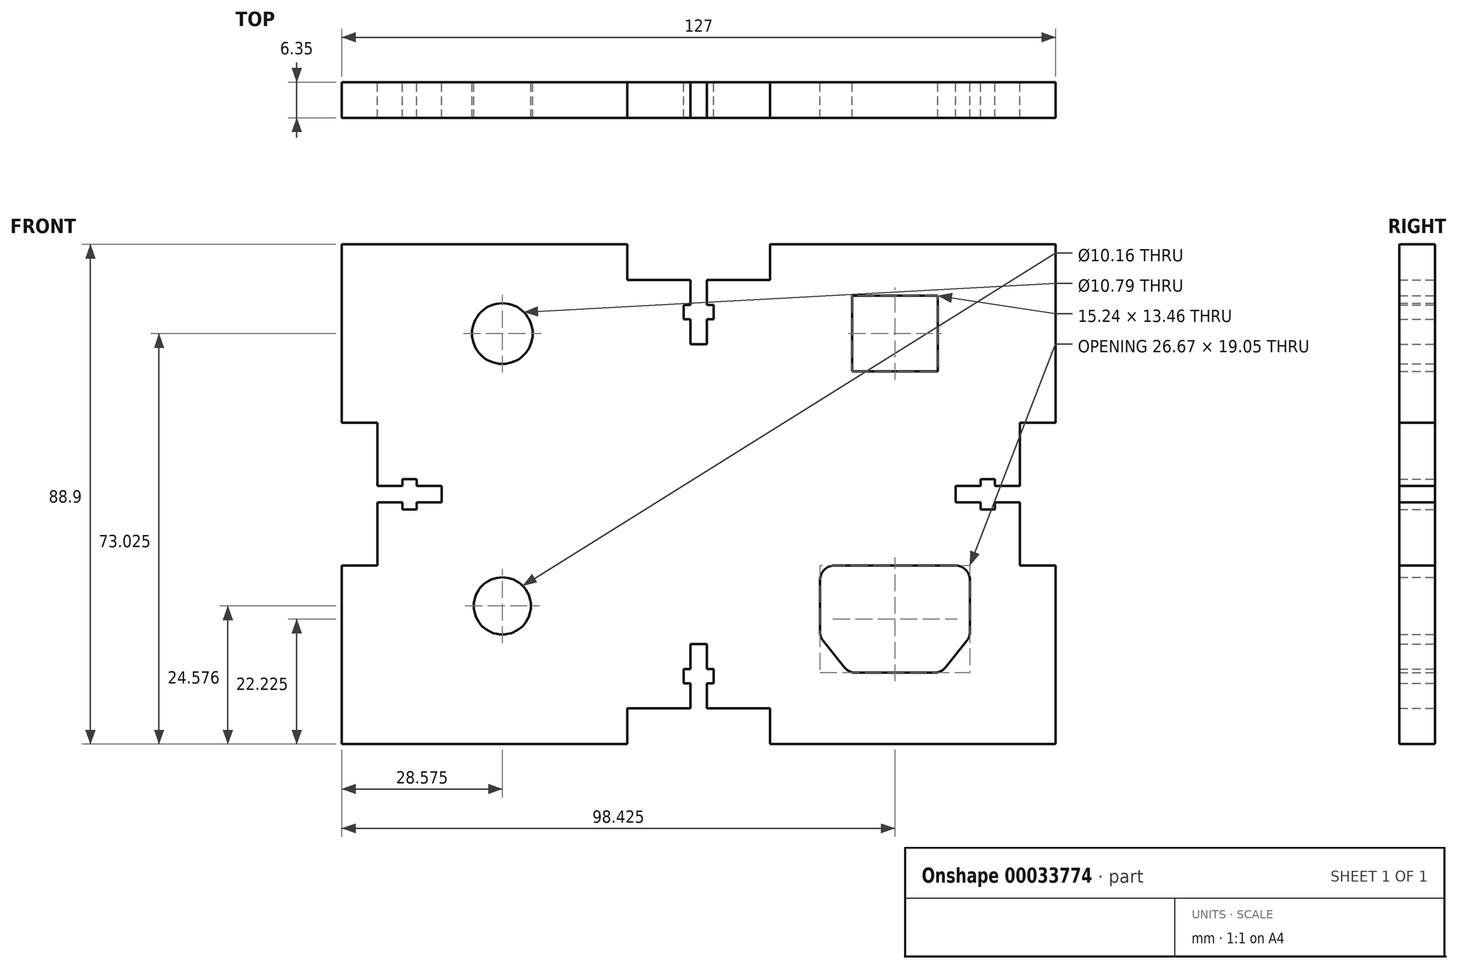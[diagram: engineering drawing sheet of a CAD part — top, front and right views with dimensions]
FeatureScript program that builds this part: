
annotation { "Feature Type Name" : "Feature", "Feature Type Description" : "" }
export const myFeature = defineFeature(function(context is Context, id is Id, definition is map)
    precondition{}
    {
        {
            var Q0;
            Q0=qCreatedBy(makeId("Front.planeOp"),FACE);
            var sketch = newSketch(context, id + "F0", { "sketchPlane" : qUnion([Q0])});
            skLineSegment(sketch, "E0.rect.bottom", {"start": v(57.15, -44.45) * mm, "end": v(12.7, -44.45) * mm});
            skLineSegment(sketch, "E0.rect.top", {"start": v(57.15, 44.45) * mm, "end": v(12.7, 44.45) * mm});
            skPoint(sketch, "E0.rect.middle", {"position": v(0, 0) * mm});
            skLineSegment(sketch, "E1.0", {"start": v(57.15, 38.1) * mm, "end": v(-57.15, 38.1) * mm, "construction": true});
            skLineSegment(sketch, "E1.1", {"start": v(57.15, -38.1) * mm, "end": v(57.15, 38.1) * mm, "construction": true});
            skLineSegment(sketch, "E1.2", {"start": v(57.15, -38.1) * mm, "end": v(-57.15, -38.1) * mm, "construction": true});
            skLineSegment(sketch, "E2", {"start": v(-63.5, 0) * mm, "end": v(-57.15, 0) * mm, "construction": true});
            skLineSegment(sketch, "E3", {"start": v(0, 44.45) * mm, "end": v(0, -44.45) * mm, "construction": true});
            skLineSegment(sketch, "E4.MirrorCS", {"start": v(12.7, 44.45) * mm, "end": v(12.7, -44.45) * mm, "construction": true});
            skLineSegment(sketch, "E5.0", {"start": v(-63.5, -12.7) * mm, "end": v(63.5, -12.7) * mm, "construction": true});
            skLineSegment(sketch, "E6.MirrorCS", {"start": v(-63.5, 12.7) * mm, "end": v(-57.15, 12.7) * mm, "construction": true});
            skLineSegment(sketch, "E7", {"start": v(-63.5, 12.7) * mm, "end": v(-57.15, 12.7) * mm});
            skLineSegment(sketch, "E8", {"start": v(-63.5, -12.7) * mm, "end": v(-57.15, -12.7) * mm});
            skPoint(sketch, "E9.orphan", {"position": v(-63.5, -44.45) * mm});
            skPoint(sketch, "E10.orphan", {"position": v(-63.5, 44.45) * mm});
            skLineSegment(sketch, "E11.MirrorCS", {"start": v(63.5, -12.7) * mm, "end": v(57.15, -12.7) * mm});
            skLineSegment(sketch, "E12.MirrorCS", {"start": v(63.5, 12.7) * mm, "end": v(57.15, 12.7) * mm});
            skPoint(sketch, "E13.orphan", {"position": v(63.5, 44.45) * mm});
            skPoint(sketch, "E14.orphan", {"position": v(63.5, -44.45) * mm});
            skLineSegment(sketch, "E15", {"start": v(-12.7, 44.45) * mm, "end": v(-12.7, 38.1) * mm});
            skLineSegment(sketch, "E16", {"start": v(-12.7, 38.1) * mm, "end": v(-1.46, 38.1) * mm});
            skLineSegment(sketch, "E17", {"start": v(12.7, 38.1) * mm, "end": v(12.7, 44.45) * mm});
            skLineSegment(sketch, "E18.MirrorCS", {"start": v(-12.7, -44.45) * mm, "end": v(-12.7, -38.1) * mm});
            skLineSegment(sketch, "E19.MirrorCS", {"start": v(-12.7, -38.1) * mm, "end": v(-1.46, -38.1) * mm});
            skLineSegment(sketch, "E20.MirrorCS", {"start": v(12.7, -38.1) * mm, "end": v(12.7, -44.45) * mm});
            skLineSegment(sketch, "E21.trimOffspring", {"start": v(-12.7, 44.45) * mm, "end": v(-57.15, 44.45) * mm});
            skLineSegment(sketch, "E22.trimOffspring", {"start": v(-12.7, -44.45) * mm, "end": v(-57.15, -44.45) * mm});
            skLineSegment(sketch, "E23", {"start": v(-12.7, 26.67) * mm, "end": v(12.7, 26.67) * mm, "construction": true});
            skLineSegment(sketch, "E24.0", {"start": v(-1.46, 44.45) * mm, "end": v(-1.46, -44.45) * mm, "construction": true});
            skLineSegment(sketch, "E25.0", {"start": v(-2.7, 44.45) * mm, "end": v(-2.7, -44.45) * mm, "construction": true});
            skLineSegment(sketch, "E26.MirrorCS", {"start": v(1.46, 44.45) * mm, "end": v(1.46, -44.45) * mm, "construction": true});
            skLineSegment(sketch, "E27.MirrorCS", {"start": v(2.7, 44.45) * mm, "end": v(2.7, -44.45) * mm, "construction": true});
            skLineSegment(sketch, "E28", {"start": v(-12.7, 26.67) * mm, "end": v(-12.7, -44.45) * mm, "construction": true});
            skLineSegment(sketch, "E29", {"start": v(-12.7, 38.1) * mm, "end": v(-12.7, 26.67) * mm, "construction": true});
            skLineSegment(sketch, "E30", {"start": v(-12.7, 32.39) * mm, "end": v(12.7, 32.39) * mm, "construction": true});
            skLineSegment(sketch, "E31.0", {"start": v(-12.7, 31.12) * mm, "end": v(12.7, 31.12) * mm, "construction": true});
            skLineSegment(sketch, "E32.MirrorCS", {"start": v(-12.7, 33.66) * mm, "end": v(12.7, 33.66) * mm, "construction": true});
            skLineSegment(sketch, "E33", {"start": v(-1.46, 38.1) * mm, "end": v(-1.46, 33.66) * mm});
            skPoint(sketch, "E33.endSnap0", {"position": v(0, 33.66) * mm});
            skLineSegment(sketch, "E34", {"start": v(-1.46, 33.66) * mm, "end": v(-2.7, 33.66) * mm});
            skLineSegment(sketch, "E35", {"start": v(-2.7, 33.66) * mm, "end": v(-2.7, 31.12) * mm});
            skLineSegment(sketch, "E36", {"start": v(-2.7, 31.12) * mm, "end": v(-1.46, 31.12) * mm});
            skLineSegment(sketch, "E37", {"start": v(-1.46, 31.12) * mm, "end": v(-1.46, 26.67) * mm});
            skLineSegment(sketch, "E38", {"start": v(-1.46, 26.67) * mm, "end": v(1.46, 26.67) * mm});
            skLineSegment(sketch, "E39", {"start": v(1.46, 26.67) * mm, "end": v(1.46, 31.12) * mm});
            skLineSegment(sketch, "E40", {"start": v(1.46, 31.12) * mm, "end": v(2.7, 31.12) * mm});
            skLineSegment(sketch, "E41", {"start": v(2.7, 31.12) * mm, "end": v(2.7, 33.66) * mm});
            skLineSegment(sketch, "E42", {"start": v(2.7, 33.66) * mm, "end": v(1.46, 33.66) * mm});
            skLineSegment(sketch, "E43", {"start": v(1.46, 33.66) * mm, "end": v(1.46, 38.1) * mm});
            skLineSegment(sketch, "E44.trimOffspring", {"start": v(1.46, 38.1) * mm, "end": v(12.7, 38.1) * mm});
            skLineSegment(sketch, "E45.MirrorCS", {"start": v(1.46, -33.66) * mm, "end": v(1.46, -38.1) * mm});
            skLineSegment(sketch, "E46.MirrorCS", {"start": v(2.7, -33.66) * mm, "end": v(1.46, -33.66) * mm});
            skLineSegment(sketch, "E47.MirrorCS", {"start": v(2.7, -31.12) * mm, "end": v(2.7, -33.66) * mm});
            skLineSegment(sketch, "E48.MirrorCS", {"start": v(1.46, -31.12) * mm, "end": v(2.7, -31.12) * mm});
            skLineSegment(sketch, "E49.MirrorCS", {"start": v(1.46, -26.67) * mm, "end": v(1.46, -31.12) * mm});
            skLineSegment(sketch, "E50.MirrorCS", {"start": v(-1.46, -26.67) * mm, "end": v(1.46, -26.67) * mm});
            skLineSegment(sketch, "E51.MirrorCS", {"start": v(-1.46, -31.12) * mm, "end": v(-1.46, -26.67) * mm});
            skLineSegment(sketch, "E52.MirrorCS", {"start": v(-2.7, -31.12) * mm, "end": v(-1.46, -31.12) * mm});
            skLineSegment(sketch, "E53.MirrorCS", {"start": v(-2.7, -33.66) * mm, "end": v(-2.7, -31.12) * mm});
            skLineSegment(sketch, "E54.MirrorCS", {"start": v(-1.46, -33.66) * mm, "end": v(-2.7, -33.66) * mm});
            skLineSegment(sketch, "E55.MirrorCS", {"start": v(-1.46, -38.1) * mm, "end": v(-1.46, -33.66) * mm});
            skLineSegment(sketch, "E56.trimOffspring", {"start": v(1.46, -38.1) * mm, "end": v(12.7, -38.1) * mm});
            skLineSegment(sketch, "E57", {"start": v(-57.15, 0) * mm, "end": v(-57.15, 38.1) * mm, "construction": true});
            skLineSegment(sketch, "E58", {"start": v(-34.93, 0) * mm, "end": v(63.5, 0) * mm, "construction": true});
            skLineSegment(sketch, "E59", {"start": v(-34.93, 44.45) * mm, "end": v(-34.93, -44.45) * mm, "construction": true});
            skLineSegment(sketch, "E60", {"start": v(34.93, 44.45) * mm, "end": v(34.93, -44.45) * mm});
            skLineSegment(sketch, "E61", {"start": v(-34.93, 28.57) * mm, "end": v(-57.15, 28.57) * mm, "construction": true});
            skPoint(sketch, "E61.startSnap0", {"position": v(-57.15, 28.57) * mm});
            skLineSegment(sketch, "E62", {"start": v(-34.93, 28.57) * mm, "end": v(57.15, 28.58) * mm, "construction": true});
            skLineSegment(sketch, "E63", {"start": v(57.15, -28.57) * mm, "end": v(-57.15, -28.58) * mm, "construction": true});
            skLineSegment(sketch, "E64.rect.bottom", {"start": v(42.55, 21.84) * mm, "end": v(27.3, 21.84) * mm});
            skLineSegment(sketch, "E64.rect.top", {"start": v(42.55, 35.3) * mm, "end": v(27.3, 35.3) * mm});
            skLineSegment(sketch, "E64.rect.left", {"start": v(42.55, 21.84) * mm, "end": v(42.55, 35.3) * mm});
            skLineSegment(sketch, "E64.rect.right", {"start": v(27.3, 21.84) * mm, "end": v(27.3, 35.3) * mm});
            skPoint(sketch, "E64.rect.middle", {"position": v(34.93, 28.58) * mm});
            skLineSegment(sketch, "E65", {"start": v(24.13, -12.7) * mm, "end": v(45.72, -12.7) * mm});
            skLineSegment(sketch, "E66", {"start": v(48.26, -15.24) * mm, "end": v(48.26, -24.5) * mm});
            skLineSegment(sketch, "E67.MirrorCS", {"start": v(21.6, -15.24) * mm, "end": v(21.6, -24.5) * mm});
            skLineSegment(sketch, "E68", {"start": v(21.6, -25.4) * mm, "end": v(48.26, -25.4) * mm, "construction": true});
            skLineSegment(sketch, "E69.0", {"start": v(34.93, -31.75) * mm, "end": v(41.96, -31.75) * mm});
            skLineSegment(sketch, "E70", {"start": v(43.94, -30.8) * mm, "end": v(47.7, -26.1) * mm});
            skLineSegment(sketch, "E71.MirrorCS", {"start": v(34.93, -31.75) * mm, "end": v(27.9, -31.75) * mm});
            skLineSegment(sketch, "E72.MirrorCS", {"start": v(25.9, -30.8) * mm, "end": v(22.15, -26.1) * mm});
            skPoint(sketch, "E73.visualSharp", {"position": v(21.6, -12.7) * mm});
            skArc(sketch, "E73.filletArc", {"start": v(24.13, -12.7) * mm, "mid": v(22.33, -13.44) * mm, "end": v(21.6, -15.24) * mm});
            skPoint(sketch, "E74.visualSharp", {"position": v(48.26, -12.7) * mm});
            skArc(sketch, "E74.filletArc", {"start": v(48.26, -15.24) * mm, "mid": v(47.52, -13.44) * mm, "end": v(45.72, -12.7) * mm});
            skPoint(sketch, "E75.visualSharp", {"position": v(48.26, -25.4) * mm});
            skArc(sketch, "E75.filletArc", {"start": v(47.7, -26.1) * mm, "mid": v(48.12, -25.35) * mm, "end": v(48.26, -24.5) * mm});
            skPoint(sketch, "E76.visualSharp", {"position": v(43.18, -31.75) * mm});
            skArc(sketch, "E76.filletArc", {"start": v(41.96, -31.75) * mm, "mid": v(43.06, -31.5) * mm, "end": v(43.94, -30.8) * mm});
            skPoint(sketch, "E77.visualSharp", {"position": v(26.67, -31.75) * mm});
            skArc(sketch, "E77.filletArc", {"start": v(25.9, -30.8) * mm, "mid": v(26.8, -31.5) * mm, "end": v(27.9, -31.75) * mm});
            skPoint(sketch, "E78.visualSharp", {"position": v(21.6, -25.4) * mm});
            skArc(sketch, "E78.filletArc", {"start": v(21.6, -24.5) * mm, "mid": v(21.73, -25.35) * mm, "end": v(22.15, -26.1) * mm});
            skCircle(sketch, "E79", {"center": v(-34.93, 28.57) * mm, "radius": 5.4 * mm});
            skLineSegment(sketch, "E80", {"start": v(21.6, -19.87) * mm, "end": v(-34.93, -19.87) * mm, "construction": true});
            skCircle(sketch, "E81", {"center": v(-34.93, -19.87) * mm, "radius": 5.08 * mm});
            skLineSegment(sketch, "E82", {"start": v(-57.15, 44.45) * mm, "end": v(-63.5, 44.45) * mm});
            skLineSegment(sketch, "E83", {"start": v(-63.5, 12.7) * mm, "end": v(-63.5, 44.45) * mm});
            skLineSegment(sketch, "E84", {"start": v(-63.5, -12.7) * mm, "end": v(-63.5, -44.45) * mm});
            skLineSegment(sketch, "E85", {"start": v(-57.15, -44.45) * mm, "end": v(-63.5, -44.45) * mm});
            skLineSegment(sketch, "E86", {"start": v(57.15, -44.45) * mm, "end": v(63.5, -44.45) * mm});
            skLineSegment(sketch, "E87", {"start": v(63.5, -44.45) * mm, "end": v(63.5, -12.7) * mm});
            skLineSegment(sketch, "E88", {"start": v(63.5, 12.7) * mm, "end": v(63.5, 44.45) * mm});
            skLineSegment(sketch, "E89", {"start": v(63.5, 44.45) * mm, "end": v(57.15, 44.45) * mm});
            skLineSegment(sketch, "E90", {"start": v(-57.15, -12.7) * mm, "end": v(-57.15, -2.7) * mm});
            skPoint(sketch, "E91.center.orphan", {"position": v(-60.33, 0) * mm});
            skLineSegment(sketch, "E92", {"start": v(57.15, 12.7) * mm, "end": v(57.15, 1.46) * mm});
            skPoint(sketch, "E93.MirrorCS.end.orphan", {"position": v(57.15, 12.7) * mm});
            skPoint(sketch, "E93.MirrorCS.start.orphan", {"position": v(50.8, 12.7) * mm});
            skPoint(sketch, "E94.MirrorCS.start.orphan", {"position": v(50.8, -12.7) * mm});
            skPoint(sketch, "E95.orphan", {"position": v(57.15, -12.7) * mm});
            skPoint(sketch, "E96.MirrorCS.end.orphan", {"position": v(63.5, 12.7) * mm});
            skPoint(sketch, "E97.MirrorCS.start.orphan", {"position": v(-50.8, -12.7) * mm});
            skPoint(sketch, "E98.MirrorCS.end.orphan", {"position": v(-57.15, 12.7) * mm});
            skPoint(sketch, "E99.MirrorCS.end.orphan", {"position": v(-57.15, -12.7) * mm});
            skLineSegment(sketch, "E100", {"start": v(-34.93, 0) * mm, "end": v(-57.15, 0) * mm, "construction": true});
            skLineSegment(sketch, "E101.0", {"start": v(-34.93, 1.46) * mm, "end": v(-57.15, 1.46) * mm, "construction": true});
            skLineSegment(sketch, "E102.MirrorCS", {"start": v(-34.93, -1.46) * mm, "end": v(-57.15, -1.46) * mm, "construction": true});
            skLineSegment(sketch, "E103.0", {"start": v(-34.93, 2.7) * mm, "end": v(-57.15, 2.7) * mm, "construction": true});
            skLineSegment(sketch, "E104.MirrorCS", {"start": v(-34.93, -2.7) * mm, "end": v(-57.15, -2.7) * mm, "construction": true});
            skLineSegment(sketch, "E105", {"start": v(-45.72, 12.7) * mm, "end": v(-45.72, -12.7) * mm, "construction": true});
            skLineSegment(sketch, "E106.trimOffspring", {"start": v(-45.72, 12.7) * mm, "end": v(63.5, 12.7) * mm, "construction": true});
            skLineSegment(sketch, "E107", {"start": v(-57.15, 12.7) * mm, "end": v(-45.72, 12.7) * mm, "construction": true});
            skLineSegment(sketch, "E108", {"start": v(-52.7, -1.46) * mm, "end": v(-57.15, -1.46) * mm});
            skLineSegment(sketch, "E109.trimOffspring", {"start": v(-57.15, 1.46) * mm, "end": v(-57.15, 12.7) * mm});
            skLineSegment(sketch, "E110", {"start": v(-57.15, -1.46) * mm, "end": v(-57.15, -2.7) * mm});
            skLineSegment(sketch, "E111.trimOffspring", {"start": v(57.15, -1.46) * mm, "end": v(57.15, -12.7) * mm});
            skLineSegment(sketch, "E112", {"start": v(-51.44, 12.7) * mm, "end": v(-51.44, -12.7) * mm, "construction": true});
            skLineSegment(sketch, "E113.0", {"start": v(-52.7, 12.7) * mm, "end": v(-52.7, -12.7) * mm, "construction": true});
            skLineSegment(sketch, "E114.MirrorCS", {"start": v(-50.17, 12.7) * mm, "end": v(-50.17, -12.7) * mm, "construction": true});
            skLineSegment(sketch, "E115", {"start": v(-57.15, 1.46) * mm, "end": v(-52.7, 1.46) * mm});
            skLineSegment(sketch, "E116", {"start": v(-52.7, 1.46) * mm, "end": v(-52.7, 2.7) * mm});
            skLineSegment(sketch, "E117", {"start": v(-52.7, 2.7) * mm, "end": v(-50.17, 2.7) * mm});
            skLineSegment(sketch, "E118", {"start": v(-50.17, 2.7) * mm, "end": v(-50.17, 1.46) * mm});
            skLineSegment(sketch, "E119", {"start": v(-50.17, 1.46) * mm, "end": v(-45.72, 1.46) * mm});
            skLineSegment(sketch, "E120", {"start": v(-45.72, 1.46) * mm, "end": v(-45.72, -1.46) * mm});
            skLineSegment(sketch, "E121", {"start": v(-45.72, -1.46) * mm, "end": v(-50.17, -1.46) * mm});
            skLineSegment(sketch, "E122", {"start": v(-50.17, -1.46) * mm, "end": v(-50.17, -2.7) * mm});
            skLineSegment(sketch, "E123", {"start": v(-50.17, -2.7) * mm, "end": v(-52.7, -2.7) * mm});
            skLineSegment(sketch, "E124", {"start": v(-52.7, -2.7) * mm, "end": v(-52.7, -1.46) * mm});
            skLineSegment(sketch, "E125.MirrorCS", {"start": v(52.7, -1.46) * mm, "end": v(57.15, -1.46) * mm});
            skLineSegment(sketch, "E126.MirrorCS", {"start": v(52.7, -2.7) * mm, "end": v(52.7, -1.46) * mm});
            skLineSegment(sketch, "E127.MirrorCS", {"start": v(50.17, -2.7) * mm, "end": v(52.7, -2.7) * mm});
            skLineSegment(sketch, "E128.MirrorCS", {"start": v(50.17, -1.46) * mm, "end": v(50.17, -2.7) * mm});
            skLineSegment(sketch, "E129.MirrorCS", {"start": v(45.72, -1.46) * mm, "end": v(50.17, -1.46) * mm});
            skLineSegment(sketch, "E130.MirrorCS", {"start": v(45.72, 1.46) * mm, "end": v(45.72, -1.46) * mm});
            skLineSegment(sketch, "E131.MirrorCS", {"start": v(50.17, 1.46) * mm, "end": v(45.72, 1.46) * mm});
            skLineSegment(sketch, "E132.MirrorCS", {"start": v(50.17, 2.7) * mm, "end": v(50.17, 1.46) * mm});
            skLineSegment(sketch, "E133.MirrorCS", {"start": v(52.7, 2.7) * mm, "end": v(50.17, 2.7) * mm});
            skLineSegment(sketch, "E134.MirrorCS", {"start": v(52.7, 1.46) * mm, "end": v(52.7, 2.7) * mm});
            skLineSegment(sketch, "E135.MirrorCS", {"start": v(57.15, 1.46) * mm, "end": v(52.7, 1.46) * mm});
            skSolve(sketch);
        }
        {
            var Q0;
            Q0 = qSketchRegion(id + "F0", true);
            var Q1;
            Q1=makeQuery(id+"F0.imprint","IMPRINT",FACE,{"disambiguationData":[TD([[makeQuery(id+"F0.imprint","IMPRINT",EDGE,{"derivedFrom":sQuery(id+"F0.wireOp",EDGE,"E0.rect.right")}),-1.0]])]});
            extrude(context, id + "F1", {"entities" : qUnion([Q0, Q1]), "depth" : 6.35 * mm});
        }
    });
